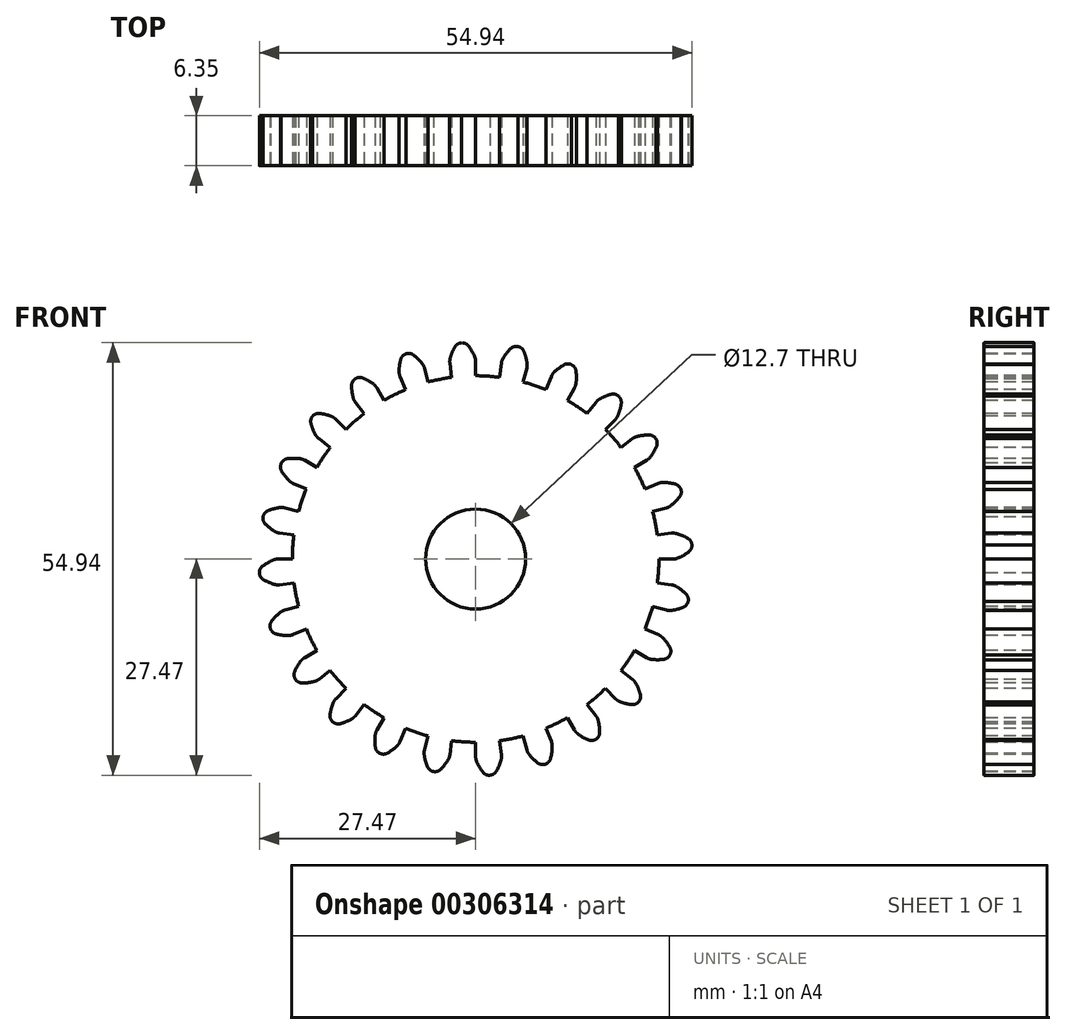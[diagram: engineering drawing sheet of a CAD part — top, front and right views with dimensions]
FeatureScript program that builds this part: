
annotation { "Feature Type Name" : "Feature", "Feature Type Description" : "" }
export const myFeature = defineFeature(function(context is Context, id is Id, definition is map)
    precondition{}
    {
        {
            var Q0;
            Q0=qCreatedBy(makeId("Front.planeOp"),FACE);
            var sketch = newSketch(context, id + "F0", { "sketchPlane" : qUnion([Q0])});
            skCircle(sketch, "E0", {"center": v(0, 0) * mm, "radius": 23.28 * mm});
            skArc(sketch, "E1", {"start": v(-0.13, 25.73) * mm, "mid": v(-0.48, 26.42) * mm, "end": v(-0.9, 27.07) * mm});
            skLineSegment(sketch, "E2", {"start": v(0, 25.1) * mm, "end": v(0, 23.28) * mm});
            skLineSegment(sketch, "E3", {"start": v(-1.77, 27.47) * mm, "end": v(-1.8, 27.47) * mm});
            skArc(sketch, "E4.MirrorCS", {"start": v(-3.23, 25.52) * mm, "mid": v(-2.97, 26.26) * mm, "end": v(-2.63, 26.96) * mm});
            skLineSegment(sketch, "E5.MirrorCS", {"start": v(-3.28, 24.88) * mm, "end": v(-3.04, 23.08) * mm});
            skLineSegment(sketch, "E6.MirrorCS", {"start": v(-1.83, 27.46) * mm, "end": v(-1.8, 27.47) * mm});
            skPoint(sketch, "E7.visualSharp", {"position": v(-3.32, 25.18) * mm});
            skArc(sketch, "E7.filletArc", {"start": v(-3.23, 25.52) * mm, "mid": v(-3.29, 25.2) * mm, "end": v(-3.28, 24.88) * mm});
            skPoint(sketch, "E8.visualSharp", {"position": v(0, 25.4) * mm});
            skArc(sketch, "E8.filletArc", {"start": v(0, 25.1) * mm, "mid": v(-0.03, 25.42) * mm, "end": v(-0.13, 25.73) * mm});
            skPoint(sketch, "E9.visualSharp", {"position": v(-2.34, 27.42) * mm});
            skArc(sketch, "E9.filletArc", {"start": v(-1.83, 27.46) * mm, "mid": v(-2.3, 27.3) * mm, "end": v(-2.63, 26.96) * mm});
            skPoint(sketch, "E10.visualSharp", {"position": v(-1.26, 27.5) * mm});
            skArc(sketch, "E10.filletArc", {"start": v(-0.9, 27.07) * mm, "mid": v(-1.29, 27.37) * mm, "end": v(-1.77, 27.47) * mm});
            skLineSegment(sketch, "E11.1.0", {"start": v(-9.6, 23.19) * mm, "end": v(-8.9, 21.5) * mm});
            skLineSegment(sketch, "E11.1.1", {"start": v(-6.5, 24.24) * mm, "end": v(-6.03, 22.49) * mm});
            skArc(sketch, "E11.1.2", {"start": v(-6.78, 24.82) * mm, "mid": v(-7.3, 25.4) * mm, "end": v(-7.88, 25.91) * mm});
            skArc(sketch, "E11.1.3", {"start": v(-8.88, 26.05) * mm, "mid": v(-9.29, 25.78) * mm, "end": v(-9.52, 25.36) * mm});
            skArc(sketch, "E11.1.4", {"start": v(-7.88, 25.91) * mm, "mid": v(-8.33, 26.1) * mm, "end": v(-8.81, 26.08) * mm});
            skArc(sketch, "E11.1.5", {"start": v(-9.73, 23.82) * mm, "mid": v(-9.67, 24.6) * mm, "end": v(-9.52, 25.36) * mm});
            skArc(sketch, "E11.1.6", {"start": v(-9.73, 23.82) * mm, "mid": v(-9.7, 23.5) * mm, "end": v(-9.6, 23.19) * mm});
            skArc(sketch, "E11.1.7", {"start": v(-6.5, 24.24) * mm, "mid": v(-6.61, 24.54) * mm, "end": v(-6.78, 24.82) * mm});
            skLineSegment(sketch, "E11.2.0", {"start": v(-15.28, 19.91) * mm, "end": v(-14.17, 18.47) * mm});
            skLineSegment(sketch, "E11.2.1", {"start": v(-12.55, 21.73) * mm, "end": v(-11.64, 20.16) * mm});
            skArc(sketch, "E11.2.2", {"start": v(-12.97, 22.21) * mm, "mid": v(-13.62, 22.64) * mm, "end": v(-14.32, 22.99) * mm});
            skArc(sketch, "E11.2.3", {"start": v(-15.32, 22.87) * mm, "mid": v(-15.64, 22.5) * mm, "end": v(-15.76, 22.03) * mm});
            skArc(sketch, "E11.2.4", {"start": v(-14.32, 22.99) * mm, "mid": v(-14.8, 23.06) * mm, "end": v(-15.26, 22.9) * mm});
            skArc(sketch, "E11.2.5", {"start": v(-15.56, 20.49) * mm, "mid": v(-15.7, 21.25) * mm, "end": v(-15.76, 22.03) * mm});
            skArc(sketch, "E11.2.6", {"start": v(-15.56, 20.49) * mm, "mid": v(-15.45, 20.19) * mm, "end": v(-15.28, 19.91) * mm});
            skArc(sketch, "E11.2.7", {"start": v(-12.55, 21.73) * mm, "mid": v(-12.74, 22) * mm, "end": v(-12.97, 22.21) * mm});
            skLineSegment(sketch, "E12.2.3.0", {"start": v(-19.91, 15.28) * mm, "end": v(-18.47, 14.17) * mm});
            skLineSegment(sketch, "E12.3.3.0", {"start": v(-17.75, 17.75) * mm, "end": v(-16.46, 16.46) * mm});
            skArc(sketch, "E12.6.3.0", {"start": v(-18.28, 18.1) * mm, "mid": v(-19.02, 18.34) * mm, "end": v(-19.78, 18.5) * mm});
            skArc(sketch, "E12.10.3.0", {"start": v(-20.72, 18.12) * mm, "mid": v(-20.93, 17.69) * mm, "end": v(-20.92, 17.2) * mm});
            skArc(sketch, "E12.14.3.0", {"start": v(-19.78, 18.5) * mm, "mid": v(-20.27, 18.45) * mm, "end": v(-20.67, 18.17) * mm});
            skArc(sketch, "E12.18.3.0", {"start": v(-20.33, 15.76) * mm, "mid": v(-20.67, 16.46) * mm, "end": v(-20.92, 17.2) * mm});
            skArc(sketch, "E12.22.3.0", {"start": v(-20.33, 15.76) * mm, "mid": v(-20.15, 15.5) * mm, "end": v(-19.91, 15.28) * mm});
            skArc(sketch, "E12.26.3.0", {"start": v(-17.75, 17.75) * mm, "mid": v(-18, 17.95) * mm, "end": v(-18.28, 18.1) * mm});
            skLineSegment(sketch, "E12.2.4.0", {"start": v(-23.19, 9.6) * mm, "end": v(-21.5, 8.9) * mm});
            skLineSegment(sketch, "E12.3.4.0", {"start": v(-21.73, 12.55) * mm, "end": v(-20.16, 11.64) * mm});
            skArc(sketch, "E12.6.4.0", {"start": v(-22.34, 12.75) * mm, "mid": v(-23.12, 12.8) * mm, "end": v(-23.9, 12.75) * mm});
            skArc(sketch, "E12.10.4.0", {"start": v(-24.7, 12.14) * mm, "mid": v(-24.8, 11.67) * mm, "end": v(-24.66, 11.2) * mm});
            skArc(sketch, "E12.14.4.0", {"start": v(-23.9, 12.75) * mm, "mid": v(-24.35, 12.57) * mm, "end": v(-24.67, 12.2) * mm});
            skArc(sketch, "E12.18.4.0", {"start": v(-23.72, 9.96) * mm, "mid": v(-24.23, 10.55) * mm, "end": v(-24.66, 11.2) * mm});
            skArc(sketch, "E12.22.4.0", {"start": v(-23.72, 9.96) * mm, "mid": v(-23.47, 9.76) * mm, "end": v(-23.19, 9.6) * mm});
            skArc(sketch, "E12.26.4.0", {"start": v(-21.73, 12.55) * mm, "mid": v(-22.03, 12.68) * mm, "end": v(-22.34, 12.75) * mm});
            skLineSegment(sketch, "E12.2.5.0", {"start": v(-24.88, 3.28) * mm, "end": v(-23.08, 3.04) * mm});
            skLineSegment(sketch, "E12.3.5.0", {"start": v(-24.24, 6.5) * mm, "end": v(-22.49, 6.03) * mm});
            skArc(sketch, "E12.6.5.0", {"start": v(-24.88, 6.53) * mm, "mid": v(-25.64, 6.38) * mm, "end": v(-26.38, 6.13) * mm});
            skArc(sketch, "E12.10.5.0", {"start": v(-27, 5.34) * mm, "mid": v(-26.97, 4.85) * mm, "end": v(-26.72, 4.44) * mm});
            skArc(sketch, "E12.14.5.0", {"start": v(-26.38, 6.13) * mm, "mid": v(-26.77, 5.84) * mm, "end": v(-26.99, 5.4) * mm});
            skArc(sketch, "E12.18.5.0", {"start": v(-25.49, 3.49) * mm, "mid": v(-26.13, 3.92) * mm, "end": v(-26.72, 4.44) * mm});
            skArc(sketch, "E12.22.5.0", {"start": v(-25.49, 3.49) * mm, "mid": v(-25.2, 3.35) * mm, "end": v(-24.88, 3.28) * mm});
            skArc(sketch, "E12.26.5.0", {"start": v(-24.24, 6.5) * mm, "mid": v(-24.56, 6.55) * mm, "end": v(-24.88, 6.53) * mm});
            skLineSegment(sketch, "E12.2.6.0", {"start": v(-24.88, -3.28) * mm, "end": v(-23.08, -3.04) * mm});
            skLineSegment(sketch, "E12.3.6.0", {"start": v(-25.1, 0) * mm, "end": v(-23.28, 0) * mm});
            skArc(sketch, "E12.6.6.0", {"start": v(-25.73, -0.13) * mm, "mid": v(-26.42, -0.48) * mm, "end": v(-27.07, -0.9) * mm});
            skArc(sketch, "E12.10.6.0", {"start": v(-27.46, -1.83) * mm, "mid": v(-27.3, -2.3) * mm, "end": v(-26.96, -2.63) * mm});
            skArc(sketch, "E12.14.6.0", {"start": v(-27.07, -0.9) * mm, "mid": v(-27.37, -1.29) * mm, "end": v(-27.47, -1.77) * mm});
            skArc(sketch, "E12.18.6.0", {"start": v(-25.52, -3.23) * mm, "mid": v(-26.26, -2.97) * mm, "end": v(-26.96, -2.63) * mm});
            skArc(sketch, "E12.22.6.0", {"start": v(-25.52, -3.23) * mm, "mid": v(-25.2, -3.29) * mm, "end": v(-24.88, -3.28) * mm});
            skArc(sketch, "E12.26.6.0", {"start": v(-25.1, 0) * mm, "mid": v(-25.42, -0.03) * mm, "end": v(-25.73, -0.13) * mm});
            skLineSegment(sketch, "E12.2.7.0", {"start": v(-23.19, -9.6) * mm, "end": v(-21.5, -8.9) * mm});
            skLineSegment(sketch, "E12.3.7.0", {"start": v(-24.24, -6.5) * mm, "end": v(-22.49, -6.03) * mm});
            skArc(sketch, "E12.6.7.0", {"start": v(-24.82, -6.78) * mm, "mid": v(-25.4, -7.3) * mm, "end": v(-25.91, -7.88) * mm});
            skArc(sketch, "E12.10.7.0", {"start": v(-26.05, -8.88) * mm, "mid": v(-25.78, -9.29) * mm, "end": v(-25.36, -9.52) * mm});
            skArc(sketch, "E12.14.7.0", {"start": v(-25.91, -7.88) * mm, "mid": v(-26.1, -8.33) * mm, "end": v(-26.08, -8.81) * mm});
            skArc(sketch, "E12.18.7.0", {"start": v(-23.82, -9.73) * mm, "mid": v(-24.6, -9.67) * mm, "end": v(-25.36, -9.52) * mm});
            skArc(sketch, "E12.22.7.0", {"start": v(-23.82, -9.73) * mm, "mid": v(-23.5, -9.7) * mm, "end": v(-23.19, -9.6) * mm});
            skArc(sketch, "E12.26.7.0", {"start": v(-24.24, -6.5) * mm, "mid": v(-24.54, -6.61) * mm, "end": v(-24.82, -6.78) * mm});
            skLineSegment(sketch, "E12.2.8.0", {"start": v(-19.91, -15.28) * mm, "end": v(-18.47, -14.17) * mm});
            skLineSegment(sketch, "E12.3.8.0", {"start": v(-21.73, -12.55) * mm, "end": v(-20.16, -11.64) * mm});
            skArc(sketch, "E12.6.8.0", {"start": v(-22.21, -12.97) * mm, "mid": v(-22.64, -13.62) * mm, "end": v(-22.99, -14.32) * mm});
            skArc(sketch, "E12.10.8.0", {"start": v(-22.87, -15.32) * mm, "mid": v(-22.5, -15.64) * mm, "end": v(-22.03, -15.76) * mm});
            skArc(sketch, "E12.14.8.0", {"start": v(-22.99, -14.32) * mm, "mid": v(-23.06, -14.8) * mm, "end": v(-22.9, -15.26) * mm});
            skArc(sketch, "E12.18.8.0", {"start": v(-20.49, -15.56) * mm, "mid": v(-21.25, -15.7) * mm, "end": v(-22.03, -15.76) * mm});
            skArc(sketch, "E12.22.8.0", {"start": v(-20.49, -15.56) * mm, "mid": v(-20.19, -15.45) * mm, "end": v(-19.91, -15.28) * mm});
            skArc(sketch, "E12.26.8.0", {"start": v(-21.73, -12.55) * mm, "mid": v(-22, -12.74) * mm, "end": v(-22.21, -12.97) * mm});
            skLineSegment(sketch, "E12.2.9.0", {"start": v(-15.28, -19.91) * mm, "end": v(-14.17, -18.47) * mm});
            skLineSegment(sketch, "E12.3.9.0", {"start": v(-17.75, -17.75) * mm, "end": v(-16.46, -16.46) * mm});
            skArc(sketch, "E12.6.9.0", {"start": v(-18.1, -18.28) * mm, "mid": v(-18.34, -19.02) * mm, "end": v(-18.5, -19.78) * mm});
            skArc(sketch, "E12.10.9.0", {"start": v(-18.12, -20.72) * mm, "mid": v(-17.69, -20.93) * mm, "end": v(-17.2, -20.92) * mm});
            skArc(sketch, "E12.14.9.0", {"start": v(-18.5, -19.78) * mm, "mid": v(-18.45, -20.27) * mm, "end": v(-18.17, -20.67) * mm});
            skArc(sketch, "E12.18.9.0", {"start": v(-15.76, -20.33) * mm, "mid": v(-16.46, -20.67) * mm, "end": v(-17.2, -20.92) * mm});
            skArc(sketch, "E12.22.9.0", {"start": v(-15.76, -20.33) * mm, "mid": v(-15.5, -20.15) * mm, "end": v(-15.28, -19.91) * mm});
            skArc(sketch, "E12.26.9.0", {"start": v(-17.75, -17.75) * mm, "mid": v(-17.95, -18) * mm, "end": v(-18.1, -18.28) * mm});
            skLineSegment(sketch, "E12.2.10.0", {"start": v(-9.6, -23.19) * mm, "end": v(-8.9, -21.5) * mm});
            skLineSegment(sketch, "E12.3.10.0", {"start": v(-12.55, -21.73) * mm, "end": v(-11.64, -20.16) * mm});
            skArc(sketch, "E12.6.10.0", {"start": v(-12.75, -22.34) * mm, "mid": v(-12.8, -23.12) * mm, "end": v(-12.75, -23.9) * mm});
            skArc(sketch, "E12.10.10.0", {"start": v(-12.14, -24.7) * mm, "mid": v(-11.67, -24.8) * mm, "end": v(-11.2, -24.66) * mm});
            skArc(sketch, "E12.14.10.0", {"start": v(-12.75, -23.9) * mm, "mid": v(-12.57, -24.35) * mm, "end": v(-12.2, -24.67) * mm});
            skArc(sketch, "E12.18.10.0", {"start": v(-9.96, -23.72) * mm, "mid": v(-10.55, -24.23) * mm, "end": v(-11.2, -24.66) * mm});
            skArc(sketch, "E12.22.10.0", {"start": v(-9.96, -23.72) * mm, "mid": v(-9.76, -23.47) * mm, "end": v(-9.6, -23.19) * mm});
            skArc(sketch, "E12.26.10.0", {"start": v(-12.55, -21.73) * mm, "mid": v(-12.68, -22.03) * mm, "end": v(-12.75, -22.34) * mm});
            skLineSegment(sketch, "E12.2.11.0", {"start": v(-3.28, -24.88) * mm, "end": v(-3.04, -23.08) * mm});
            skLineSegment(sketch, "E12.3.11.0", {"start": v(-6.5, -24.24) * mm, "end": v(-6.03, -22.49) * mm});
            skArc(sketch, "E12.6.11.0", {"start": v(-6.53, -24.88) * mm, "mid": v(-6.38, -25.64) * mm, "end": v(-6.13, -26.38) * mm});
            skArc(sketch, "E12.10.11.0", {"start": v(-5.34, -27) * mm, "mid": v(-4.85, -26.97) * mm, "end": v(-4.44, -26.72) * mm});
            skArc(sketch, "E12.14.11.0", {"start": v(-6.13, -26.38) * mm, "mid": v(-5.84, -26.77) * mm, "end": v(-5.4, -26.99) * mm});
            skArc(sketch, "E12.18.11.0", {"start": v(-3.49, -25.49) * mm, "mid": v(-3.92, -26.13) * mm, "end": v(-4.44, -26.72) * mm});
            skArc(sketch, "E12.22.11.0", {"start": v(-3.49, -25.49) * mm, "mid": v(-3.35, -25.2) * mm, "end": v(-3.28, -24.88) * mm});
            skArc(sketch, "E12.26.11.0", {"start": v(-6.5, -24.24) * mm, "mid": v(-6.55, -24.56) * mm, "end": v(-6.53, -24.88) * mm});
            skLineSegment(sketch, "E12.2.12.0", {"start": v(3.28, -24.88) * mm, "end": v(3.04, -23.08) * mm});
            skLineSegment(sketch, "E12.3.12.0", {"start": v(0, -25.1) * mm, "end": v(0, -23.28) * mm});
            skArc(sketch, "E12.6.12.0", {"start": v(0.13, -25.73) * mm, "mid": v(0.48, -26.42) * mm, "end": v(0.9, -27.07) * mm});
            skArc(sketch, "E12.10.12.0", {"start": v(1.83, -27.46) * mm, "mid": v(2.3, -27.3) * mm, "end": v(2.63, -26.96) * mm});
            skArc(sketch, "E12.14.12.0", {"start": v(0.9, -27.07) * mm, "mid": v(1.29, -27.37) * mm, "end": v(1.77, -27.47) * mm});
            skArc(sketch, "E12.18.12.0", {"start": v(3.23, -25.52) * mm, "mid": v(2.97, -26.26) * mm, "end": v(2.63, -26.96) * mm});
            skArc(sketch, "E12.22.12.0", {"start": v(3.23, -25.52) * mm, "mid": v(3.29, -25.2) * mm, "end": v(3.28, -24.88) * mm});
            skArc(sketch, "E12.26.12.0", {"start": v(0, -25.1) * mm, "mid": v(0.03, -25.42) * mm, "end": v(0.13, -25.73) * mm});
            skLineSegment(sketch, "E12.2.13.0", {"start": v(9.6, -23.19) * mm, "end": v(8.9, -21.5) * mm});
            skLineSegment(sketch, "E12.3.13.0", {"start": v(6.5, -24.24) * mm, "end": v(6.03, -22.49) * mm});
            skArc(sketch, "E12.6.13.0", {"start": v(6.78, -24.82) * mm, "mid": v(7.3, -25.4) * mm, "end": v(7.88, -25.91) * mm});
            skArc(sketch, "E12.10.13.0", {"start": v(8.88, -26.05) * mm, "mid": v(9.29, -25.78) * mm, "end": v(9.52, -25.36) * mm});
            skArc(sketch, "E12.14.13.0", {"start": v(7.88, -25.91) * mm, "mid": v(8.33, -26.1) * mm, "end": v(8.81, -26.08) * mm});
            skArc(sketch, "E12.18.13.0", {"start": v(9.73, -23.82) * mm, "mid": v(9.67, -24.6) * mm, "end": v(9.52, -25.36) * mm});
            skArc(sketch, "E12.22.13.0", {"start": v(9.73, -23.82) * mm, "mid": v(9.7, -23.5) * mm, "end": v(9.6, -23.19) * mm});
            skArc(sketch, "E12.26.13.0", {"start": v(6.5, -24.24) * mm, "mid": v(6.61, -24.54) * mm, "end": v(6.78, -24.82) * mm});
            skLineSegment(sketch, "E12.2.14.0", {"start": v(15.28, -19.91) * mm, "end": v(14.17, -18.47) * mm});
            skLineSegment(sketch, "E12.3.14.0", {"start": v(12.55, -21.73) * mm, "end": v(11.64, -20.16) * mm});
            skArc(sketch, "E12.6.14.0", {"start": v(12.97, -22.21) * mm, "mid": v(13.62, -22.64) * mm, "end": v(14.32, -22.99) * mm});
            skArc(sketch, "E12.10.14.0", {"start": v(15.32, -22.87) * mm, "mid": v(15.64, -22.5) * mm, "end": v(15.76, -22.03) * mm});
            skArc(sketch, "E12.14.14.0", {"start": v(14.32, -22.99) * mm, "mid": v(14.8, -23.06) * mm, "end": v(15.26, -22.9) * mm});
            skArc(sketch, "E12.18.14.0", {"start": v(15.56, -20.49) * mm, "mid": v(15.7, -21.25) * mm, "end": v(15.76, -22.03) * mm});
            skArc(sketch, "E12.22.14.0", {"start": v(15.56, -20.49) * mm, "mid": v(15.45, -20.19) * mm, "end": v(15.28, -19.91) * mm});
            skArc(sketch, "E12.26.14.0", {"start": v(12.55, -21.73) * mm, "mid": v(12.74, -22) * mm, "end": v(12.97, -22.21) * mm});
            skLineSegment(sketch, "E12.2.15.0", {"start": v(19.91, -15.28) * mm, "end": v(18.47, -14.17) * mm});
            skLineSegment(sketch, "E12.3.15.0", {"start": v(17.75, -17.75) * mm, "end": v(16.46, -16.46) * mm});
            skArc(sketch, "E12.6.15.0", {"start": v(18.28, -18.1) * mm, "mid": v(19.02, -18.34) * mm, "end": v(19.78, -18.5) * mm});
            skArc(sketch, "E12.10.15.0", {"start": v(20.72, -18.12) * mm, "mid": v(20.93, -17.69) * mm, "end": v(20.92, -17.2) * mm});
            skArc(sketch, "E12.14.15.0", {"start": v(19.78, -18.5) * mm, "mid": v(20.27, -18.45) * mm, "end": v(20.67, -18.17) * mm});
            skArc(sketch, "E12.18.15.0", {"start": v(20.33, -15.76) * mm, "mid": v(20.67, -16.46) * mm, "end": v(20.92, -17.2) * mm});
            skArc(sketch, "E12.22.15.0", {"start": v(20.33, -15.76) * mm, "mid": v(20.15, -15.5) * mm, "end": v(19.91, -15.28) * mm});
            skArc(sketch, "E12.26.15.0", {"start": v(17.75, -17.75) * mm, "mid": v(18, -17.95) * mm, "end": v(18.28, -18.1) * mm});
            skLineSegment(sketch, "E13.2.16.0", {"start": v(23.19, -9.6) * mm, "end": v(21.5, -8.9) * mm});
            skLineSegment(sketch, "E13.3.16.0", {"start": v(21.73, -12.55) * mm, "end": v(20.16, -11.64) * mm});
            skArc(sketch, "E13.6.16.0", {"start": v(22.34, -12.75) * mm, "mid": v(23.12, -12.8) * mm, "end": v(23.9, -12.75) * mm});
            skArc(sketch, "E13.10.16.0", {"start": v(24.7, -12.14) * mm, "mid": v(24.8, -11.67) * mm, "end": v(24.66, -11.2) * mm});
            skArc(sketch, "E13.14.16.0", {"start": v(23.9, -12.75) * mm, "mid": v(24.35, -12.57) * mm, "end": v(24.67, -12.2) * mm});
            skArc(sketch, "E13.18.16.0", {"start": v(23.72, -9.96) * mm, "mid": v(24.23, -10.55) * mm, "end": v(24.66, -11.2) * mm});
            skArc(sketch, "E13.22.16.0", {"start": v(23.72, -9.96) * mm, "mid": v(23.47, -9.76) * mm, "end": v(23.19, -9.6) * mm});
            skArc(sketch, "E13.26.16.0", {"start": v(21.73, -12.55) * mm, "mid": v(22.03, -12.68) * mm, "end": v(22.34, -12.75) * mm});
            skLineSegment(sketch, "E13.2.17.0", {"start": v(24.88, -3.28) * mm, "end": v(23.08, -3.04) * mm});
            skLineSegment(sketch, "E13.3.17.0", {"start": v(24.24, -6.5) * mm, "end": v(22.49, -6.03) * mm});
            skArc(sketch, "E13.6.17.0", {"start": v(24.88, -6.53) * mm, "mid": v(25.64, -6.38) * mm, "end": v(26.38, -6.13) * mm});
            skArc(sketch, "E13.10.17.0", {"start": v(27, -5.34) * mm, "mid": v(26.97, -4.85) * mm, "end": v(26.72, -4.44) * mm});
            skArc(sketch, "E13.14.17.0", {"start": v(26.38, -6.13) * mm, "mid": v(26.77, -5.84) * mm, "end": v(26.99, -5.4) * mm});
            skArc(sketch, "E13.18.17.0", {"start": v(25.49, -3.49) * mm, "mid": v(26.13, -3.92) * mm, "end": v(26.72, -4.44) * mm});
            skArc(sketch, "E13.22.17.0", {"start": v(25.49, -3.49) * mm, "mid": v(25.2, -3.35) * mm, "end": v(24.88, -3.28) * mm});
            skArc(sketch, "E13.26.17.0", {"start": v(24.24, -6.5) * mm, "mid": v(24.56, -6.55) * mm, "end": v(24.88, -6.53) * mm});
            skLineSegment(sketch, "E13.2.18.0", {"start": v(24.88, 3.28) * mm, "end": v(23.08, 3.04) * mm});
            skLineSegment(sketch, "E13.3.18.0", {"start": v(25.1, 0) * mm, "end": v(23.28, 0) * mm});
            skArc(sketch, "E13.6.18.0", {"start": v(25.73, 0.13) * mm, "mid": v(26.42, 0.48) * mm, "end": v(27.07, 0.9) * mm});
            skArc(sketch, "E13.10.18.0", {"start": v(27.46, 1.83) * mm, "mid": v(27.3, 2.3) * mm, "end": v(26.96, 2.63) * mm});
            skArc(sketch, "E13.14.18.0", {"start": v(27.07, 0.9) * mm, "mid": v(27.37, 1.29) * mm, "end": v(27.47, 1.77) * mm});
            skArc(sketch, "E13.18.18.0", {"start": v(25.52, 3.23) * mm, "mid": v(26.26, 2.97) * mm, "end": v(26.96, 2.63) * mm});
            skArc(sketch, "E13.22.18.0", {"start": v(25.52, 3.23) * mm, "mid": v(25.2, 3.29) * mm, "end": v(24.88, 3.28) * mm});
            skArc(sketch, "E13.26.18.0", {"start": v(25.1, 0) * mm, "mid": v(25.42, 0.03) * mm, "end": v(25.73, 0.13) * mm});
            skLineSegment(sketch, "E13.2.19.0", {"start": v(23.19, 9.6) * mm, "end": v(21.5, 8.9) * mm});
            skLineSegment(sketch, "E13.3.19.0", {"start": v(24.24, 6.5) * mm, "end": v(22.49, 6.03) * mm});
            skArc(sketch, "E13.6.19.0", {"start": v(24.82, 6.78) * mm, "mid": v(25.4, 7.3) * mm, "end": v(25.91, 7.88) * mm});
            skArc(sketch, "E13.10.19.0", {"start": v(26.05, 8.88) * mm, "mid": v(25.78, 9.29) * mm, "end": v(25.36, 9.52) * mm});
            skArc(sketch, "E13.14.19.0", {"start": v(25.91, 7.88) * mm, "mid": v(26.1, 8.33) * mm, "end": v(26.08, 8.81) * mm});
            skArc(sketch, "E13.18.19.0", {"start": v(23.82, 9.73) * mm, "mid": v(24.6, 9.67) * mm, "end": v(25.36, 9.52) * mm});
            skArc(sketch, "E13.22.19.0", {"start": v(23.82, 9.73) * mm, "mid": v(23.5, 9.7) * mm, "end": v(23.19, 9.6) * mm});
            skArc(sketch, "E13.26.19.0", {"start": v(24.24, 6.5) * mm, "mid": v(24.54, 6.61) * mm, "end": v(24.82, 6.78) * mm});
            skLineSegment(sketch, "E13.2.20.0", {"start": v(19.91, 15.28) * mm, "end": v(18.47, 14.17) * mm});
            skLineSegment(sketch, "E13.3.20.0", {"start": v(21.73, 12.55) * mm, "end": v(20.16, 11.64) * mm});
            skArc(sketch, "E13.6.20.0", {"start": v(22.21, 12.97) * mm, "mid": v(22.64, 13.62) * mm, "end": v(22.99, 14.32) * mm});
            skArc(sketch, "E13.10.20.0", {"start": v(22.87, 15.32) * mm, "mid": v(22.5, 15.64) * mm, "end": v(22.03, 15.76) * mm});
            skArc(sketch, "E13.14.20.0", {"start": v(22.99, 14.32) * mm, "mid": v(23.06, 14.8) * mm, "end": v(22.9, 15.26) * mm});
            skArc(sketch, "E13.18.20.0", {"start": v(20.49, 15.56) * mm, "mid": v(21.25, 15.7) * mm, "end": v(22.03, 15.76) * mm});
            skArc(sketch, "E13.22.20.0", {"start": v(20.49, 15.56) * mm, "mid": v(20.19, 15.45) * mm, "end": v(19.91, 15.28) * mm});
            skArc(sketch, "E13.26.20.0", {"start": v(21.73, 12.55) * mm, "mid": v(22, 12.74) * mm, "end": v(22.21, 12.97) * mm});
            skLineSegment(sketch, "E13.2.21.0", {"start": v(15.28, 19.91) * mm, "end": v(14.17, 18.47) * mm});
            skLineSegment(sketch, "E13.3.21.0", {"start": v(17.75, 17.75) * mm, "end": v(16.46, 16.46) * mm});
            skArc(sketch, "E13.6.21.0", {"start": v(18.1, 18.28) * mm, "mid": v(18.34, 19.02) * mm, "end": v(18.5, 19.78) * mm});
            skArc(sketch, "E13.10.21.0", {"start": v(18.12, 20.72) * mm, "mid": v(17.69, 20.93) * mm, "end": v(17.2, 20.92) * mm});
            skArc(sketch, "E13.14.21.0", {"start": v(18.5, 19.78) * mm, "mid": v(18.45, 20.27) * mm, "end": v(18.17, 20.67) * mm});
            skArc(sketch, "E13.18.21.0", {"start": v(15.76, 20.33) * mm, "mid": v(16.46, 20.67) * mm, "end": v(17.2, 20.92) * mm});
            skArc(sketch, "E13.22.21.0", {"start": v(15.76, 20.33) * mm, "mid": v(15.5, 20.15) * mm, "end": v(15.28, 19.91) * mm});
            skArc(sketch, "E13.26.21.0", {"start": v(17.75, 17.75) * mm, "mid": v(17.95, 18) * mm, "end": v(18.1, 18.28) * mm});
            skLineSegment(sketch, "E13.2.22.0", {"start": v(9.6, 23.19) * mm, "end": v(8.9, 21.5) * mm});
            skLineSegment(sketch, "E13.3.22.0", {"start": v(12.55, 21.73) * mm, "end": v(11.64, 20.16) * mm});
            skArc(sketch, "E13.6.22.0", {"start": v(12.75, 22.34) * mm, "mid": v(12.8, 23.12) * mm, "end": v(12.75, 23.9) * mm});
            skArc(sketch, "E13.10.22.0", {"start": v(12.14, 24.7) * mm, "mid": v(11.67, 24.8) * mm, "end": v(11.2, 24.66) * mm});
            skArc(sketch, "E13.14.22.0", {"start": v(12.75, 23.9) * mm, "mid": v(12.57, 24.35) * mm, "end": v(12.2, 24.67) * mm});
            skArc(sketch, "E13.18.22.0", {"start": v(9.96, 23.72) * mm, "mid": v(10.55, 24.23) * mm, "end": v(11.2, 24.66) * mm});
            skArc(sketch, "E13.22.22.0", {"start": v(9.96, 23.72) * mm, "mid": v(9.76, 23.47) * mm, "end": v(9.6, 23.19) * mm});
            skArc(sketch, "E13.26.22.0", {"start": v(12.55, 21.73) * mm, "mid": v(12.68, 22.03) * mm, "end": v(12.75, 22.34) * mm});
            skLineSegment(sketch, "E13.2.23.0", {"start": v(3.28, 24.88) * mm, "end": v(3.04, 23.08) * mm});
            skLineSegment(sketch, "E13.3.23.0", {"start": v(6.5, 24.24) * mm, "end": v(6.03, 22.49) * mm});
            skArc(sketch, "E13.6.23.0", {"start": v(6.53, 24.88) * mm, "mid": v(6.38, 25.64) * mm, "end": v(6.13, 26.38) * mm});
            skArc(sketch, "E13.10.23.0", {"start": v(5.34, 27) * mm, "mid": v(4.85, 26.97) * mm, "end": v(4.44, 26.72) * mm});
            skArc(sketch, "E13.14.23.0", {"start": v(6.13, 26.38) * mm, "mid": v(5.84, 26.77) * mm, "end": v(5.4, 26.99) * mm});
            skArc(sketch, "E13.18.23.0", {"start": v(3.49, 25.49) * mm, "mid": v(3.92, 26.13) * mm, "end": v(4.44, 26.72) * mm});
            skArc(sketch, "E13.22.23.0", {"start": v(3.49, 25.49) * mm, "mid": v(3.35, 25.2) * mm, "end": v(3.28, 24.88) * mm});
            skArc(sketch, "E13.26.23.0", {"start": v(6.5, 24.24) * mm, "mid": v(6.55, 24.56) * mm, "end": v(6.53, 24.88) * mm});
            skSolve(sketch);
        }
        {
            var Q0;
            {var subQ0=sQuery(id+"F0.wireOp",EDGE,"E0");var subQ33=makeQuery(id+"F0.imprint","IMPRINT",VERTEX,{"disambiguationData":[OD(34.0)],"derivedFrom":subQ0});Q0=makeQuery(id+"F0.imprint","IMPRINT",FACE,{"disambiguationData":[TD([[makeQuery(id+"F0.imprint","IMPRINT",EDGE,{"disambiguationData":[TD([[subQ33,1.0]])],"derivedFrom":subQ0}),1.0]])]});}
            cPlane(context, id + "F1", {"entities" : qUnion([Q0]), "cplaneType" : CPlaneType.OFFSET, "offset" : 6.35 * mm, "width" : 152.4 * mm, "height" : 152.4 * mm});
        }
        {
            var Q0;
            Q0=qCreatedBy(id+"F1.planeOp",FACE);
            var sketch = newSketch(context, id + "F2", { "sketchPlane" : qUnion([Q0])});
            skArc(sketch, "E14.0.0", {"start": v(23.28, 0) * mm, "mid": v(23.23, 1.52) * mm, "end": v(23.08, 3.04) * mm});
            skArc(sketch, "E14.0.1", {"start": v(23.08, 3.04) * mm, "mid": v(22.83, 4.54) * mm, "end": v(22.49, 6.03) * mm});
            skArc(sketch, "E14.0.2", {"start": v(22.49, 6.03) * mm, "mid": v(22.04, 7.48) * mm, "end": v(21.5, 8.9) * mm});
            skArc(sketch, "E14.0.3", {"start": v(21.5, 8.9) * mm, "mid": v(20.88, 10.3) * mm, "end": v(20.16, 11.64) * mm});
            skArc(sketch, "E14.0.4", {"start": v(20.16, 11.64) * mm, "mid": v(19.36, 12.93) * mm, "end": v(18.47, 14.17) * mm});
            skArc(sketch, "E14.0.5", {"start": v(18.47, 14.17) * mm, "mid": v(17.5, 15.35) * mm, "end": v(16.46, 16.46) * mm});
            skArc(sketch, "E14.0.6", {"start": v(16.46, 16.46) * mm, "mid": v(15.35, 17.5) * mm, "end": v(14.17, 18.47) * mm});
            skArc(sketch, "E14.0.7", {"start": v(14.17, 18.47) * mm, "mid": v(12.93, 19.36) * mm, "end": v(11.64, 20.16) * mm});
            skArc(sketch, "E14.0.8", {"start": v(11.64, 20.16) * mm, "mid": v(10.3, 20.88) * mm, "end": v(8.9, 21.5) * mm});
            skArc(sketch, "E14.0.9", {"start": v(8.9, 21.5) * mm, "mid": v(7.48, 22.04) * mm, "end": v(6.03, 22.49) * mm});
            skArc(sketch, "E14.0.10", {"start": v(6.03, 22.49) * mm, "mid": v(4.54, 22.83) * mm, "end": v(3.04, 23.08) * mm});
            skArc(sketch, "E14.0.11", {"start": v(3.04, 23.08) * mm, "mid": v(1.52, 23.23) * mm, "end": v(0, 23.28) * mm});
            skArc(sketch, "E14.0.12", {"start": v(0, 23.28) * mm, "mid": v(-1.52, 23.23) * mm, "end": v(-3.04, 23.08) * mm});
            skArc(sketch, "E14.0.13", {"start": v(-3.04, 23.08) * mm, "mid": v(-4.54, 22.83) * mm, "end": v(-6.03, 22.49) * mm});
            skArc(sketch, "E14.0.14", {"start": v(-6.03, 22.49) * mm, "mid": v(-7.48, 22.04) * mm, "end": v(-8.9, 21.5) * mm});
            skArc(sketch, "E14.0.15", {"start": v(-8.9, 21.5) * mm, "mid": v(-10.3, 20.88) * mm, "end": v(-11.64, 20.16) * mm});
            skArc(sketch, "E14.0.16", {"start": v(-11.64, 20.16) * mm, "mid": v(-12.93, 19.36) * mm, "end": v(-14.17, 18.47) * mm});
            skArc(sketch, "E14.0.17", {"start": v(-14.17, 18.47) * mm, "mid": v(-15.35, 17.5) * mm, "end": v(-16.46, 16.46) * mm});
            skArc(sketch, "E14.0.18", {"start": v(-16.46, 16.46) * mm, "mid": v(-17.5, 15.35) * mm, "end": v(-18.47, 14.17) * mm});
            skArc(sketch, "E14.0.19", {"start": v(-18.47, 14.17) * mm, "mid": v(-19.36, 12.93) * mm, "end": v(-20.16, 11.64) * mm});
            skArc(sketch, "E14.0.20", {"start": v(-20.16, 11.64) * mm, "mid": v(-20.88, 10.3) * mm, "end": v(-21.5, 8.9) * mm});
            skArc(sketch, "E14.0.21", {"start": v(-21.5, 8.9) * mm, "mid": v(-22.04, 7.48) * mm, "end": v(-22.49, 6.03) * mm});
            skArc(sketch, "E14.0.22", {"start": v(-22.49, 6.03) * mm, "mid": v(-22.83, 4.54) * mm, "end": v(-23.08, 3.04) * mm});
            skArc(sketch, "E14.0.23", {"start": v(-23.08, 3.04) * mm, "mid": v(-23.23, 1.52) * mm, "end": v(-23.28, 0) * mm});
            skArc(sketch, "E14.0.24", {"start": v(-23.28, 0) * mm, "mid": v(-23.23, -1.52) * mm, "end": v(-23.08, -3.04) * mm});
            skArc(sketch, "E14.0.25", {"start": v(-23.08, -3.04) * mm, "mid": v(-22.83, -4.54) * mm, "end": v(-22.49, -6.03) * mm});
            skArc(sketch, "E14.0.26", {"start": v(-22.49, -6.03) * mm, "mid": v(-22.04, -7.48) * mm, "end": v(-21.5, -8.9) * mm});
            skArc(sketch, "E14.0.27", {"start": v(-21.5, -8.9) * mm, "mid": v(-20.88, -10.3) * mm, "end": v(-20.16, -11.64) * mm});
            skArc(sketch, "E14.0.28", {"start": v(-20.16, -11.64) * mm, "mid": v(-19.36, -12.93) * mm, "end": v(-18.47, -14.17) * mm});
            skArc(sketch, "E14.0.29", {"start": v(-18.47, -14.17) * mm, "mid": v(-17.5, -15.35) * mm, "end": v(-16.46, -16.46) * mm});
            skArc(sketch, "E14.0.30", {"start": v(-16.46, -16.46) * mm, "mid": v(-15.35, -17.5) * mm, "end": v(-14.17, -18.47) * mm});
            skArc(sketch, "E14.0.31", {"start": v(-14.17, -18.47) * mm, "mid": v(-12.93, -19.36) * mm, "end": v(-11.64, -20.16) * mm});
            skArc(sketch, "E14.0.32", {"start": v(-11.64, -20.16) * mm, "mid": v(-10.3, -20.88) * mm, "end": v(-8.9, -21.5) * mm});
            skArc(sketch, "E14.0.33", {"start": v(-8.9, -21.5) * mm, "mid": v(-7.48, -22.04) * mm, "end": v(-6.03, -22.49) * mm});
            skArc(sketch, "E14.0.34", {"start": v(-6.03, -22.49) * mm, "mid": v(-4.54, -22.83) * mm, "end": v(-3.04, -23.08) * mm});
            skArc(sketch, "E14.0.35", {"start": v(-3.04, -23.08) * mm, "mid": v(-1.52, -23.23) * mm, "end": v(0, -23.28) * mm});
            skArc(sketch, "E14.0.36", {"start": v(0, -23.28) * mm, "mid": v(1.52, -23.23) * mm, "end": v(3.04, -23.08) * mm});
            skArc(sketch, "E14.0.37", {"start": v(3.04, -23.08) * mm, "mid": v(4.54, -22.83) * mm, "end": v(6.03, -22.49) * mm});
            skArc(sketch, "E14.0.38", {"start": v(6.03, -22.49) * mm, "mid": v(7.48, -22.04) * mm, "end": v(8.9, -21.5) * mm});
            skArc(sketch, "E14.0.39", {"start": v(8.9, -21.5) * mm, "mid": v(10.3, -20.88) * mm, "end": v(11.64, -20.16) * mm});
            skArc(sketch, "E14.0.40", {"start": v(11.64, -20.16) * mm, "mid": v(12.93, -19.36) * mm, "end": v(14.17, -18.47) * mm});
            skArc(sketch, "E14.0.41", {"start": v(14.17, -18.47) * mm, "mid": v(15.35, -17.5) * mm, "end": v(16.46, -16.46) * mm});
            skArc(sketch, "E14.0.42", {"start": v(16.46, -16.46) * mm, "mid": v(17.5, -15.35) * mm, "end": v(18.47, -14.17) * mm});
            skArc(sketch, "E14.0.43", {"start": v(18.47, -14.17) * mm, "mid": v(19.36, -12.93) * mm, "end": v(20.16, -11.64) * mm});
            skArc(sketch, "E14.0.44", {"start": v(20.16, -11.64) * mm, "mid": v(20.88, -10.3) * mm, "end": v(21.5, -8.9) * mm});
            skArc(sketch, "E14.0.45", {"start": v(21.5, -8.9) * mm, "mid": v(22.04, -7.48) * mm, "end": v(22.49, -6.03) * mm});
            skArc(sketch, "E14.0.46", {"start": v(22.49, -6.03) * mm, "mid": v(22.83, -4.54) * mm, "end": v(23.08, -3.04) * mm});
            skArc(sketch, "E14.0.47", {"start": v(23.08, -3.04) * mm, "mid": v(23.23, -1.52) * mm, "end": v(23.28, 0) * mm});
            skArc(sketch, "E15.0.0", {"start": v(-2.63, 26.96) * mm, "mid": v(-2.97, 26.26) * mm, "end": v(-3.23, 25.52) * mm});
            skArc(sketch, "E15.0.1", {"start": v(-3.23, 25.52) * mm, "mid": v(-3.29, 25.2) * mm, "end": v(-3.28, 24.88) * mm});
            skLineSegment(sketch, "E15.0.2", {"start": v(-3.28, 24.88) * mm, "end": v(-3.04, 23.08) * mm});
            skArc(sketch, "E15.0.3", {"start": v(-3.04, 23.08) * mm, "mid": v(-1.52, 23.23) * mm, "end": v(0, 23.28) * mm});
            skLineSegment(sketch, "E15.0.4", {"start": v(0, 23.28) * mm, "end": v(0, 25.1) * mm});
            skArc(sketch, "E15.0.5", {"start": v(0, 25.1) * mm, "mid": v(-0.03, 25.42) * mm, "end": v(-0.13, 25.73) * mm});
            skArc(sketch, "E15.0.6", {"start": v(-0.13, 25.73) * mm, "mid": v(-0.48, 26.42) * mm, "end": v(-0.9, 27.07) * mm});
            skArc(sketch, "E15.0.7", {"start": v(-0.9, 27.07) * mm, "mid": v(-1.29, 27.37) * mm, "end": v(-1.77, 27.47) * mm});
            skLineSegment(sketch, "E15.0.8", {"start": v(-1.77, 27.47) * mm, "end": v(-1.8, 27.47) * mm});
            skLineSegment(sketch, "E15.0.9", {"start": v(-1.8, 27.47) * mm, "end": v(-1.83, 27.46) * mm});
            skArc(sketch, "E15.0.10", {"start": v(-1.83, 27.46) * mm, "mid": v(-2.3, 27.3) * mm, "end": v(-2.63, 26.96) * mm});
            skSolve(sketch);
        }
        {
            var Q0;
            Q0=makeQuery(id+"F0.imprint","IMPRINT",FACE,{"disambiguationData":[TD([[makeQuery(id+"F0.imprint","IMPRINT",EDGE,{"derivedFrom":sQuery(id+"F0.wireOp",EDGE,"E1")}),1.0]])]});
            var Q1;
            Q1=makeQuery(id+"F2.imprint","IMPRINT",FACE,{"disambiguationData":[TD([[makeQuery(id+"F2.imprint","IMPRINT",EDGE,{"derivedFrom":sQuery(id+"F2.wireOp",EDGE,"E15.0.0")}),1.0]])]});
            loft(context, id + "F3", {"sheetProfilesArray" : [{ "sheetProfileEntities" : qUnion([Q0]) }, { "sheetProfileEntities" : qUnion([Q1]) }]});
        }
        {
            var Q0;
            Q0=qCreatedBy(id+"F1.planeOp",FACE);
            var sketch = newSketch(context, id + "F4", { "sketchPlane" : qUnion([Q0])});
            skCircle(sketch, "E16", {"center": v(0, 0) * mm, "radius": 23.28 * mm});
            skSolve(sketch);
        }
        {
            var Q0;
            Q0=makeQuery(id+"F4.imprint","IMPRINT",FACE,{"disambiguationData":[TD([[makeQuery(id+"F4.imprint","IMPRINT",EDGE,{"derivedFrom":sQuery(id+"F4.wireOp",EDGE,"E16")}),1.0]])]});
            var Q1;
            Q1=makeQuery(id+"F3.opLoft","CAP_FACE",FACE,{"disambiguationData":[OSD([makeQuery(id+"F0.imprint","IMPRINT",FACE,{"disambiguationData":[TD([[makeQuery(id+"F0.imprint","IMPRINT",EDGE,{"derivedFrom":sQuery(id+"F0.wireOp",EDGE,"E1")}),1.0]])]})])],"isStart":true});
            extrude(context, id + "F5", {"entities" : qUnion([Q0]), "operationType" : NewBodyOperationType.ADD, "endBound" : BoundingType.UP_TO_SURFACE, "oppositeDirection" : true, "endBoundEntityFace" : qUnion([Q1]), "depth" : 25.4 * mm});
        }
        {
            var Q0;
            Q0=makeQuery(id+"F3.opLoft","SWEPT_BODY",BODY,{"disambiguationData":[OSD([makeQuery(id+"F0.imprint","IMPRINT",FACE,{"disambiguationData":[TD([[makeQuery(id+"F0.imprint","IMPRINT",EDGE,{"derivedFrom":sQuery(id+"F0.wireOp",EDGE,"E1")}),1.0]])]}),makeQuery(id+"F2.imprint","IMPRINT",FACE,{"disambiguationData":[TD([[makeQuery(id+"F2.imprint","IMPRINT",EDGE,{"derivedFrom":sQuery(id+"F2.wireOp",EDGE,"E15.0.0")}),1.0]])]})])]});
            var Q1;
            Q1=makeQuery(id+"F5.opExtrude","SWEPT_FACE",FACE,{"disambiguationData":[OSD([sQuery(id+"F4.wireOp",EDGE,"E16")])]});
            circularPattern(context, id + "F6", {"entities" : qUnion([Q0]), "axis" : qUnion([Q1]), "angle" : 360 * degree, "instanceCount" : 24, "equalSpace" : true});
        }
        {
            var Q0;
            Q0=makeQuery(id+"F6.opPattern","COPY",BODY,{"derivedFrom":makeQuery(id+"F3.opLoft","SWEPT_BODY",BODY,{"disambiguationData":[OSD([makeQuery(id+"F0.imprint","IMPRINT",FACE,{"disambiguationData":[TD([[makeQuery(id+"F0.imprint","IMPRINT",EDGE,{"derivedFrom":sQuery(id+"F0.wireOp",EDGE,"E1")}),1.0]])]}),makeQuery(id+"F2.imprint","IMPRINT",FACE,{"disambiguationData":[TD([[makeQuery(id+"F2.imprint","IMPRINT",EDGE,{"derivedFrom":sQuery(id+"F2.wireOp",EDGE,"E15.0.0")}),1.0]])]})])]}),"instanceName":"23"});
            var Q1;
            Q1=makeQuery(id+"F6.opPattern","COPY",BODY,{"derivedFrom":makeQuery(id+"F3.opLoft","SWEPT_BODY",BODY,{"disambiguationData":[OSD([makeQuery(id+"F0.imprint","IMPRINT",FACE,{"disambiguationData":[TD([[makeQuery(id+"F0.imprint","IMPRINT",EDGE,{"derivedFrom":sQuery(id+"F0.wireOp",EDGE,"E1")}),1.0]])]}),makeQuery(id+"F2.imprint","IMPRINT",FACE,{"disambiguationData":[TD([[makeQuery(id+"F2.imprint","IMPRINT",EDGE,{"derivedFrom":sQuery(id+"F2.wireOp",EDGE,"E15.0.0")}),1.0]])]})])]}),"instanceName":"22"});
            var Q2;
            Q2=makeQuery(id+"F6.opPattern","COPY",BODY,{"derivedFrom":makeQuery(id+"F3.opLoft","SWEPT_BODY",BODY,{"disambiguationData":[OSD([makeQuery(id+"F0.imprint","IMPRINT",FACE,{"disambiguationData":[TD([[makeQuery(id+"F0.imprint","IMPRINT",EDGE,{"derivedFrom":sQuery(id+"F0.wireOp",EDGE,"E1")}),1.0]])]}),makeQuery(id+"F2.imprint","IMPRINT",FACE,{"disambiguationData":[TD([[makeQuery(id+"F2.imprint","IMPRINT",EDGE,{"derivedFrom":sQuery(id+"F2.wireOp",EDGE,"E15.0.0")}),1.0]])]})])]}),"instanceName":"21"});
            var Q3;
            Q3=makeQuery(id+"F6.opPattern","COPY",BODY,{"derivedFrom":makeQuery(id+"F3.opLoft","SWEPT_BODY",BODY,{"disambiguationData":[OSD([makeQuery(id+"F0.imprint","IMPRINT",FACE,{"disambiguationData":[TD([[makeQuery(id+"F0.imprint","IMPRINT",EDGE,{"derivedFrom":sQuery(id+"F0.wireOp",EDGE,"E1")}),1.0]])]}),makeQuery(id+"F2.imprint","IMPRINT",FACE,{"disambiguationData":[TD([[makeQuery(id+"F2.imprint","IMPRINT",EDGE,{"derivedFrom":sQuery(id+"F2.wireOp",EDGE,"E15.0.0")}),1.0]])]})])]}),"instanceName":"20"});
            var Q4;
            Q4=makeQuery(id+"F6.opPattern","COPY",BODY,{"derivedFrom":makeQuery(id+"F3.opLoft","SWEPT_BODY",BODY,{"disambiguationData":[OSD([makeQuery(id+"F0.imprint","IMPRINT",FACE,{"disambiguationData":[TD([[makeQuery(id+"F0.imprint","IMPRINT",EDGE,{"derivedFrom":sQuery(id+"F0.wireOp",EDGE,"E1")}),1.0]])]}),makeQuery(id+"F2.imprint","IMPRINT",FACE,{"disambiguationData":[TD([[makeQuery(id+"F2.imprint","IMPRINT",EDGE,{"derivedFrom":sQuery(id+"F2.wireOp",EDGE,"E15.0.0")}),1.0]])]})])]}),"instanceName":"19"});
            var Q5;
            Q5=makeQuery(id+"F6.opPattern","COPY",BODY,{"derivedFrom":makeQuery(id+"F3.opLoft","SWEPT_BODY",BODY,{"disambiguationData":[OSD([makeQuery(id+"F0.imprint","IMPRINT",FACE,{"disambiguationData":[TD([[makeQuery(id+"F0.imprint","IMPRINT",EDGE,{"derivedFrom":sQuery(id+"F0.wireOp",EDGE,"E1")}),1.0]])]}),makeQuery(id+"F2.imprint","IMPRINT",FACE,{"disambiguationData":[TD([[makeQuery(id+"F2.imprint","IMPRINT",EDGE,{"derivedFrom":sQuery(id+"F2.wireOp",EDGE,"E15.0.0")}),1.0]])]})])]}),"instanceName":"18"});
            var Q6;
            Q6=makeQuery(id+"F6.opPattern","COPY",BODY,{"derivedFrom":makeQuery(id+"F3.opLoft","SWEPT_BODY",BODY,{"disambiguationData":[OSD([makeQuery(id+"F0.imprint","IMPRINT",FACE,{"disambiguationData":[TD([[makeQuery(id+"F0.imprint","IMPRINT",EDGE,{"derivedFrom":sQuery(id+"F0.wireOp",EDGE,"E1")}),1.0]])]}),makeQuery(id+"F2.imprint","IMPRINT",FACE,{"disambiguationData":[TD([[makeQuery(id+"F2.imprint","IMPRINT",EDGE,{"derivedFrom":sQuery(id+"F2.wireOp",EDGE,"E15.0.0")}),1.0]])]})])]}),"instanceName":"17"});
            var Q7;
            Q7=makeQuery(id+"F6.opPattern","COPY",BODY,{"derivedFrom":makeQuery(id+"F3.opLoft","SWEPT_BODY",BODY,{"disambiguationData":[OSD([makeQuery(id+"F0.imprint","IMPRINT",FACE,{"disambiguationData":[TD([[makeQuery(id+"F0.imprint","IMPRINT",EDGE,{"derivedFrom":sQuery(id+"F0.wireOp",EDGE,"E1")}),1.0]])]}),makeQuery(id+"F2.imprint","IMPRINT",FACE,{"disambiguationData":[TD([[makeQuery(id+"F2.imprint","IMPRINT",EDGE,{"derivedFrom":sQuery(id+"F2.wireOp",EDGE,"E15.0.0")}),1.0]])]})])]}),"instanceName":"16"});
            var Q8;
            Q8=makeQuery(id+"F6.opPattern","COPY",BODY,{"derivedFrom":makeQuery(id+"F3.opLoft","SWEPT_BODY",BODY,{"disambiguationData":[OSD([makeQuery(id+"F0.imprint","IMPRINT",FACE,{"disambiguationData":[TD([[makeQuery(id+"F0.imprint","IMPRINT",EDGE,{"derivedFrom":sQuery(id+"F0.wireOp",EDGE,"E1")}),1.0]])]}),makeQuery(id+"F2.imprint","IMPRINT",FACE,{"disambiguationData":[TD([[makeQuery(id+"F2.imprint","IMPRINT",EDGE,{"derivedFrom":sQuery(id+"F2.wireOp",EDGE,"E15.0.0")}),1.0]])]})])]}),"instanceName":"15"});
            var Q9;
            Q9=makeQuery(id+"F6.opPattern","COPY",BODY,{"derivedFrom":makeQuery(id+"F3.opLoft","SWEPT_BODY",BODY,{"disambiguationData":[OSD([makeQuery(id+"F0.imprint","IMPRINT",FACE,{"disambiguationData":[TD([[makeQuery(id+"F0.imprint","IMPRINT",EDGE,{"derivedFrom":sQuery(id+"F0.wireOp",EDGE,"E1")}),1.0]])]}),makeQuery(id+"F2.imprint","IMPRINT",FACE,{"disambiguationData":[TD([[makeQuery(id+"F2.imprint","IMPRINT",EDGE,{"derivedFrom":sQuery(id+"F2.wireOp",EDGE,"E15.0.0")}),1.0]])]})])]}),"instanceName":"14"});
            var Q10;
            Q10=makeQuery(id+"F6.opPattern","COPY",BODY,{"derivedFrom":makeQuery(id+"F3.opLoft","SWEPT_BODY",BODY,{"disambiguationData":[OSD([makeQuery(id+"F0.imprint","IMPRINT",FACE,{"disambiguationData":[TD([[makeQuery(id+"F0.imprint","IMPRINT",EDGE,{"derivedFrom":sQuery(id+"F0.wireOp",EDGE,"E1")}),1.0]])]}),makeQuery(id+"F2.imprint","IMPRINT",FACE,{"disambiguationData":[TD([[makeQuery(id+"F2.imprint","IMPRINT",EDGE,{"derivedFrom":sQuery(id+"F2.wireOp",EDGE,"E15.0.0")}),1.0]])]})])]}),"instanceName":"13"});
            var Q11;
            Q11=makeQuery(id+"F6.opPattern","COPY",BODY,{"derivedFrom":makeQuery(id+"F3.opLoft","SWEPT_BODY",BODY,{"disambiguationData":[OSD([makeQuery(id+"F0.imprint","IMPRINT",FACE,{"disambiguationData":[TD([[makeQuery(id+"F0.imprint","IMPRINT",EDGE,{"derivedFrom":sQuery(id+"F0.wireOp",EDGE,"E1")}),1.0]])]}),makeQuery(id+"F2.imprint","IMPRINT",FACE,{"disambiguationData":[TD([[makeQuery(id+"F2.imprint","IMPRINT",EDGE,{"derivedFrom":sQuery(id+"F2.wireOp",EDGE,"E15.0.0")}),1.0]])]})])]}),"instanceName":"12"});
            var Q12;
            Q12=makeQuery(id+"F6.opPattern","COPY",BODY,{"derivedFrom":makeQuery(id+"F3.opLoft","SWEPT_BODY",BODY,{"disambiguationData":[OSD([makeQuery(id+"F0.imprint","IMPRINT",FACE,{"disambiguationData":[TD([[makeQuery(id+"F0.imprint","IMPRINT",EDGE,{"derivedFrom":sQuery(id+"F0.wireOp",EDGE,"E1")}),1.0]])]}),makeQuery(id+"F2.imprint","IMPRINT",FACE,{"disambiguationData":[TD([[makeQuery(id+"F2.imprint","IMPRINT",EDGE,{"derivedFrom":sQuery(id+"F2.wireOp",EDGE,"E15.0.0")}),1.0]])]})])]}),"instanceName":"11"});
            var Q13;
            Q13=makeQuery(id+"F6.opPattern","COPY",BODY,{"derivedFrom":makeQuery(id+"F3.opLoft","SWEPT_BODY",BODY,{"disambiguationData":[OSD([makeQuery(id+"F0.imprint","IMPRINT",FACE,{"disambiguationData":[TD([[makeQuery(id+"F0.imprint","IMPRINT",EDGE,{"derivedFrom":sQuery(id+"F0.wireOp",EDGE,"E1")}),1.0]])]}),makeQuery(id+"F2.imprint","IMPRINT",FACE,{"disambiguationData":[TD([[makeQuery(id+"F2.imprint","IMPRINT",EDGE,{"derivedFrom":sQuery(id+"F2.wireOp",EDGE,"E15.0.0")}),1.0]])]})])]}),"instanceName":"10"});
            var Q14;
            Q14=makeQuery(id+"F6.opPattern","COPY",BODY,{"derivedFrom":makeQuery(id+"F3.opLoft","SWEPT_BODY",BODY,{"disambiguationData":[OSD([makeQuery(id+"F0.imprint","IMPRINT",FACE,{"disambiguationData":[TD([[makeQuery(id+"F0.imprint","IMPRINT",EDGE,{"derivedFrom":sQuery(id+"F0.wireOp",EDGE,"E1")}),1.0]])]}),makeQuery(id+"F2.imprint","IMPRINT",FACE,{"disambiguationData":[TD([[makeQuery(id+"F2.imprint","IMPRINT",EDGE,{"derivedFrom":sQuery(id+"F2.wireOp",EDGE,"E15.0.0")}),1.0]])]})])]}),"instanceName":"8"});
            var Q15;
            Q15=makeQuery(id+"F6.opPattern","COPY",BODY,{"derivedFrom":makeQuery(id+"F3.opLoft","SWEPT_BODY",BODY,{"disambiguationData":[OSD([makeQuery(id+"F0.imprint","IMPRINT",FACE,{"disambiguationData":[TD([[makeQuery(id+"F0.imprint","IMPRINT",EDGE,{"derivedFrom":sQuery(id+"F0.wireOp",EDGE,"E1")}),1.0]])]}),makeQuery(id+"F2.imprint","IMPRINT",FACE,{"disambiguationData":[TD([[makeQuery(id+"F2.imprint","IMPRINT",EDGE,{"derivedFrom":sQuery(id+"F2.wireOp",EDGE,"E15.0.0")}),1.0]])]})])]}),"instanceName":"9"});
            var Q16;
            Q16=makeQuery(id+"F6.opPattern","COPY",BODY,{"derivedFrom":makeQuery(id+"F3.opLoft","SWEPT_BODY",BODY,{"disambiguationData":[OSD([makeQuery(id+"F0.imprint","IMPRINT",FACE,{"disambiguationData":[TD([[makeQuery(id+"F0.imprint","IMPRINT",EDGE,{"derivedFrom":sQuery(id+"F0.wireOp",EDGE,"E1")}),1.0]])]}),makeQuery(id+"F2.imprint","IMPRINT",FACE,{"disambiguationData":[TD([[makeQuery(id+"F2.imprint","IMPRINT",EDGE,{"derivedFrom":sQuery(id+"F2.wireOp",EDGE,"E15.0.0")}),1.0]])]})])]}),"instanceName":"7"});
            var Q17;
            Q17=makeQuery(id+"F6.opPattern","COPY",BODY,{"derivedFrom":makeQuery(id+"F3.opLoft","SWEPT_BODY",BODY,{"disambiguationData":[OSD([makeQuery(id+"F0.imprint","IMPRINT",FACE,{"disambiguationData":[TD([[makeQuery(id+"F0.imprint","IMPRINT",EDGE,{"derivedFrom":sQuery(id+"F0.wireOp",EDGE,"E1")}),1.0]])]}),makeQuery(id+"F2.imprint","IMPRINT",FACE,{"disambiguationData":[TD([[makeQuery(id+"F2.imprint","IMPRINT",EDGE,{"derivedFrom":sQuery(id+"F2.wireOp",EDGE,"E15.0.0")}),1.0]])]})])]}),"instanceName":"6"});
            var Q18;
            Q18=makeQuery(id+"F6.opPattern","COPY",BODY,{"derivedFrom":makeQuery(id+"F3.opLoft","SWEPT_BODY",BODY,{"disambiguationData":[OSD([makeQuery(id+"F0.imprint","IMPRINT",FACE,{"disambiguationData":[TD([[makeQuery(id+"F0.imprint","IMPRINT",EDGE,{"derivedFrom":sQuery(id+"F0.wireOp",EDGE,"E1")}),1.0]])]}),makeQuery(id+"F2.imprint","IMPRINT",FACE,{"disambiguationData":[TD([[makeQuery(id+"F2.imprint","IMPRINT",EDGE,{"derivedFrom":sQuery(id+"F2.wireOp",EDGE,"E15.0.0")}),1.0]])]})])]}),"instanceName":"5"});
            var Q19;
            Q19=makeQuery(id+"F6.opPattern","COPY",BODY,{"derivedFrom":makeQuery(id+"F3.opLoft","SWEPT_BODY",BODY,{"disambiguationData":[OSD([makeQuery(id+"F0.imprint","IMPRINT",FACE,{"disambiguationData":[TD([[makeQuery(id+"F0.imprint","IMPRINT",EDGE,{"derivedFrom":sQuery(id+"F0.wireOp",EDGE,"E1")}),1.0]])]}),makeQuery(id+"F2.imprint","IMPRINT",FACE,{"disambiguationData":[TD([[makeQuery(id+"F2.imprint","IMPRINT",EDGE,{"derivedFrom":sQuery(id+"F2.wireOp",EDGE,"E15.0.0")}),1.0]])]})])]}),"instanceName":"4"});
            var Q20;
            Q20=makeQuery(id+"F6.opPattern","COPY",BODY,{"derivedFrom":makeQuery(id+"F3.opLoft","SWEPT_BODY",BODY,{"disambiguationData":[OSD([makeQuery(id+"F0.imprint","IMPRINT",FACE,{"disambiguationData":[TD([[makeQuery(id+"F0.imprint","IMPRINT",EDGE,{"derivedFrom":sQuery(id+"F0.wireOp",EDGE,"E1")}),1.0]])]}),makeQuery(id+"F2.imprint","IMPRINT",FACE,{"disambiguationData":[TD([[makeQuery(id+"F2.imprint","IMPRINT",EDGE,{"derivedFrom":sQuery(id+"F2.wireOp",EDGE,"E15.0.0")}),1.0]])]})])]}),"instanceName":"3"});
            var Q21;
            Q21=makeQuery(id+"F6.opPattern","COPY",BODY,{"derivedFrom":makeQuery(id+"F3.opLoft","SWEPT_BODY",BODY,{"disambiguationData":[OSD([makeQuery(id+"F0.imprint","IMPRINT",FACE,{"disambiguationData":[TD([[makeQuery(id+"F0.imprint","IMPRINT",EDGE,{"derivedFrom":sQuery(id+"F0.wireOp",EDGE,"E1")}),1.0]])]}),makeQuery(id+"F2.imprint","IMPRINT",FACE,{"disambiguationData":[TD([[makeQuery(id+"F2.imprint","IMPRINT",EDGE,{"derivedFrom":sQuery(id+"F2.wireOp",EDGE,"E15.0.0")}),1.0]])]})])]}),"instanceName":"2"});
            var Q22;
            Q22=makeQuery(id+"F6.opPattern","COPY",BODY,{"derivedFrom":makeQuery(id+"F3.opLoft","SWEPT_BODY",BODY,{"disambiguationData":[OSD([makeQuery(id+"F0.imprint","IMPRINT",FACE,{"disambiguationData":[TD([[makeQuery(id+"F0.imprint","IMPRINT",EDGE,{"derivedFrom":sQuery(id+"F0.wireOp",EDGE,"E1")}),1.0]])]}),makeQuery(id+"F2.imprint","IMPRINT",FACE,{"disambiguationData":[TD([[makeQuery(id+"F2.imprint","IMPRINT",EDGE,{"derivedFrom":sQuery(id+"F2.wireOp",EDGE,"E15.0.0")}),1.0]])]})])]}),"instanceName":"1"});
            var Q23;
            Q23=makeQuery(id+"F3.opLoft","SWEPT_BODY",BODY,{"disambiguationData":[OSD([makeQuery(id+"F0.imprint","IMPRINT",FACE,{"disambiguationData":[TD([[makeQuery(id+"F0.imprint","IMPRINT",EDGE,{"derivedFrom":sQuery(id+"F0.wireOp",EDGE,"E1")}),1.0]])]}),makeQuery(id+"F2.imprint","IMPRINT",FACE,{"disambiguationData":[TD([[makeQuery(id+"F2.imprint","IMPRINT",EDGE,{"derivedFrom":sQuery(id+"F2.wireOp",EDGE,"E15.0.0")}),1.0]])]})])]});
            booleanBodies(context, id + "F7", {"operationType" : BooleanOperationType.UNION, "tools" : qUnion([Q0, Q1, Q2, Q3, Q4, Q5, Q6, Q7, Q8, Q9, Q10, Q11, Q12, Q13, Q14, Q15, Q16, Q17, Q18, Q19, Q20, Q21, Q22, Q23])});
        }
        {
            var Q0;
            {var subQ0=makeQuery(id+"F5.boolean.opBoolean","MERGE",FACE,{"derivedFrom":[makeQuery(id+"F3.opLoft","CAP_FACE",FACE,{"disambiguationData":[OSD([makeQuery(id+"F2.imprint","IMPRINT",FACE,{"disambiguationData":[TD([[makeQuery(id+"F2.imprint","IMPRINT",EDGE,{"derivedFrom":sQuery(id+"F2.wireOp",EDGE,"E15.0.0")}),1.0]])]})])],"isStart":true}),makeQuery(id+"F5.opExtrude","CAP_FACE",FACE,{"disambiguationData":[OSD([sQuery(id+"F4.wireOp",EDGE,"E16")])],"isStart":true})]});Q0=makeQuery(id+"F7.opBoolean","MERGE",FACE,{"derivedFrom":[subQ0,makeQuery(id+"F6.opPattern","COPY",FACE,{"derivedFrom":subQ0,"instanceName":"1"}),makeQuery(id+"F6.opPattern","COPY",FACE,{"derivedFrom":subQ0,"instanceName":"2"}),makeQuery(id+"F6.opPattern","COPY",FACE,{"derivedFrom":subQ0,"instanceName":"3"}),makeQuery(id+"F6.opPattern","COPY",FACE,{"derivedFrom":subQ0,"instanceName":"4"}),makeQuery(id+"F6.opPattern","COPY",FACE,{"derivedFrom":subQ0,"instanceName":"5"}),makeQuery(id+"F6.opPattern","COPY",FACE,{"derivedFrom":subQ0,"instanceName":"6"}),makeQuery(id+"F6.opPattern","COPY",FACE,{"derivedFrom":subQ0,"instanceName":"7"}),makeQuery(id+"F6.opPattern","COPY",FACE,{"derivedFrom":subQ0,"instanceName":"8"}),makeQuery(id+"F6.opPattern","COPY",FACE,{"derivedFrom":subQ0,"instanceName":"9"}),makeQuery(id+"F6.opPattern","COPY",FACE,{"derivedFrom":subQ0,"instanceName":"10"}),makeQuery(id+"F6.opPattern","COPY",FACE,{"derivedFrom":subQ0,"instanceName":"11"}),makeQuery(id+"F6.opPattern","COPY",FACE,{"derivedFrom":subQ0,"instanceName":"12"}),makeQuery(id+"F6.opPattern","COPY",FACE,{"derivedFrom":subQ0,"instanceName":"13"}),makeQuery(id+"F6.opPattern","COPY",FACE,{"derivedFrom":subQ0,"instanceName":"14"}),makeQuery(id+"F6.opPattern","COPY",FACE,{"derivedFrom":subQ0,"instanceName":"15"}),makeQuery(id+"F6.opPattern","COPY",FACE,{"derivedFrom":subQ0,"instanceName":"16"}),makeQuery(id+"F6.opPattern","COPY",FACE,{"derivedFrom":subQ0,"instanceName":"17"}),makeQuery(id+"F6.opPattern","COPY",FACE,{"derivedFrom":subQ0,"instanceName":"18"}),makeQuery(id+"F6.opPattern","COPY",FACE,{"derivedFrom":subQ0,"instanceName":"19"}),makeQuery(id+"F6.opPattern","COPY",FACE,{"derivedFrom":subQ0,"instanceName":"20"}),makeQuery(id+"F6.opPattern","COPY",FACE,{"derivedFrom":subQ0,"instanceName":"21"}),makeQuery(id+"F6.opPattern","COPY",FACE,{"derivedFrom":subQ0,"instanceName":"22"}),makeQuery(id+"F6.opPattern","COPY",FACE,{"derivedFrom":subQ0,"instanceName":"23"})]});}
            var sketch = newSketch(context, id + "F8", { "sketchPlane" : qUnion([Q0])});
            skCircle(sketch, "E17", {"center": v(0, 0) * mm, "radius": 6.35 * mm});
            skSolve(sketch);
        }
        {
            var Q0;
            Q0 = qSketchRegion(id + "F8", true);
            extrude(context, id + "F9", {"entities" : qUnion([Q0]), "operationType" : NewBodyOperationType.REMOVE, "endBound" : BoundingType.THROUGH_ALL, "oppositeDirection" : true, "depth" : 25.4 * mm});
        }
    });
